# Revit family: HVAC_Ductwork_Airzone_Motorized-Round-Damper_CPCC1
name_source: partatom
category: Duct Accessories
revit_build: Autodesk Revit 2016 (Build: 20161004_0715(x64)
units: mm (PartAtom-declared; Revit-internal decimal feet)

## family parameters
Always vertical = Yes
Cut with Voids When Loaded = No
OmniClass Number = 23.75.70.14.34
OmniClass Title = Air Duct Accessories
Part Type = Damper
Round Connector Dimension = Use Diameter
Shared = No
Work Plane-Based = No

## types (1)
- INVALID TYPE - Use Load Family and Type Catalog instead
    Accessories Material = Plastic - AIRZONE - Gray - Matte
    Actuator Description = MCCRQ - Round damper actuator - 12V, 40mA, 250mA max, 0.8 Nm
    Ak = 0.785398
    Damper Diameter = 98 mm
    Damper Length = 210 mm
    Description = Motorized round duct damper
    Disclaimer = All information provided in this model is reviewed before being published. However, Airzone cannot guarantee this model is error-free, therefore users are strongly encouraged to check for technical documentation and updates
    Duct Diameter = 100 mm
    Effective Area = 78.54 cm²
    Finish = Aluminum
    Insulation Diameter = 108 mm
    Insulation Material = Insulation - AIRZONE -  Aluminum Finish
    Long Description = CPCC motorized round duct damper to control the air inlet of the zone when attached to an air distribution round duct.
    Main Material = Metal - AIRZONE - Aluminium - Brushed
    Manufacturer = AIRZONE
    Model = INVALID – Type not loaded via type catalog
    Product Code = INVALID – Type not loaded via type catalog
    Product Comments = Refer to technical documentation for further details
    Product Documentation Download URL = http://doc.airzone.es
    Revit Model Version = 1.0
    Type Image Comments = Image available in product documentation download
    URL = www.airzone.es
    c1 = 0.000275
    c2 = -2.55

## geometry (parser evidence)
native form markers: Sweep x3
no freeform markers — native parametric forms only
